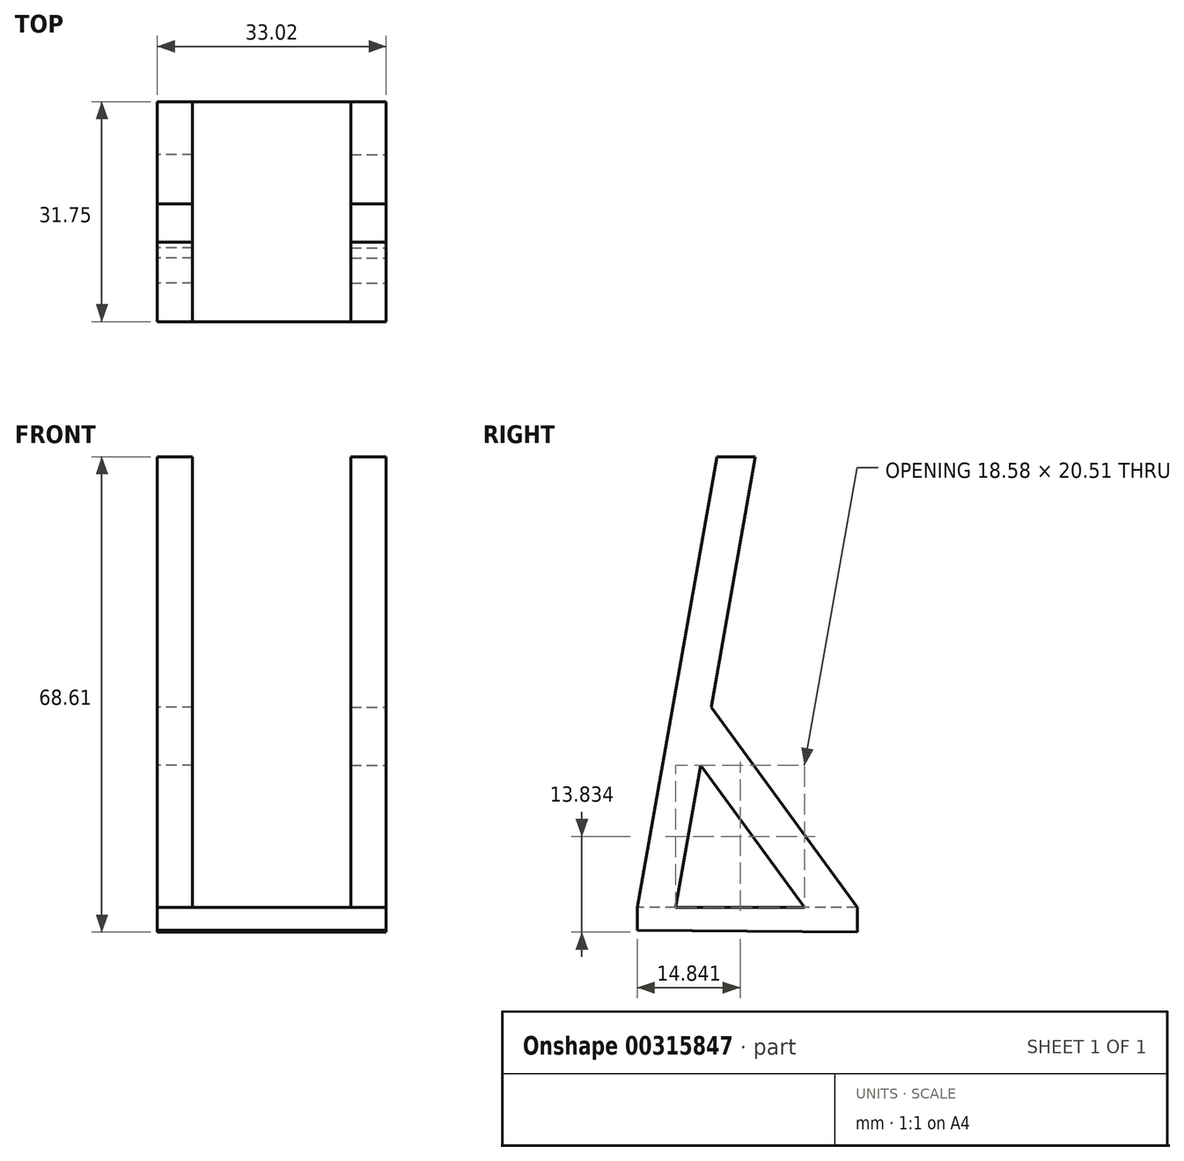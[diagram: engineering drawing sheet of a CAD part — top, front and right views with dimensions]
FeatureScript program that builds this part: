
annotation { "Feature Type Name" : "Feature", "Feature Type Description" : "" }
export const myFeature = defineFeature(function(context is Context, id is Id, definition is map)
    precondition{}
    {
        {
            var Q0;
            Q0=qCreatedBy(makeId("Right.planeOp"),FACE);
            var sketch = newSketch(context, id + "F0", { "sketchPlane" : qUnion([Q0])});
            skLineSegment(sketch, "E0", {"start": v(-16.52, -8.83) * mm, "end": v(-5.05, 56.2) * mm});
            skLineSegment(sketch, "E1", {"start": v(-10.97, -8.83) * mm, "end": v(-16.52, -8.83) * mm});
            skLineSegment(sketch, "E2", {"start": v(-10.97, -8.83) * mm, "end": v(0.5, 56.2) * mm});
            skLineSegment(sketch, "E3", {"start": v(0.5, 56.2) * mm, "end": v(-5.05, 56.2) * mm});
            skLineSegment(sketch, "E4", {"start": v(-7.35, 11.68) * mm, "end": v(7.61, -8.83) * mm});
            skLineSegment(sketch, "E5", {"start": v(15.23, -8.83) * mm, "end": v(7.61, -8.83) * mm});
            skLineSegment(sketch, "E6", {"start": v(15.23, -8.83) * mm, "end": v(-5.87, 20.1) * mm});
            skLineSegment(sketch, "E7", {"start": v(-16.52, -8.83) * mm, "end": v(-16.52, -12.16) * mm});
            skLineSegment(sketch, "E8", {"start": v(15.23, -8.83) * mm, "end": v(15.23, -12.41) * mm});
            skLineSegment(sketch, "E9", {"start": v(15.23, -12.41) * mm, "end": v(-16.52, -12.16) * mm});
            skLineSegment(sketch, "E10", {"start": v(7.61, -8.83) * mm, "end": v(-10.97, -8.83) * mm});
            skSolve(sketch);
        }
        {
            var Q0;
            Q0=makeQuery(id+"F0.imprint","IMPRINT",FACE,{"disambiguationData":[TD([[makeQuery(id+"F0.imprint","IMPRINT",EDGE,{"derivedFrom":sQuery(id+"F0.wireOp",EDGE,"E1")}),1.0]])]});
            extrude(context, id + "F1", {"entities" : qUnion([Q0]), "depth" : 16.5 * mm});
        }
        {
            var Q0;
            {var subQ0=sQuery(id+"F0.wireOp",EDGE,"E4");Q0=makeQuery(id+"F0.imprint","IMPRINT",FACE,{"disambiguationData":[TD([[makeQuery(id+"F0.imprint","IMPRINT",EDGE,{"derivedFrom":subQ0}),1.0]])]});}
            var Q1;
            Q1=makeQuery(id+"F0.imprint","IMPRINT",FACE,{"disambiguationData":[TD([[makeQuery(id+"F0.imprint","IMPRINT",EDGE,{"derivedFrom":sQuery(id+"F0.wireOp",EDGE,"E0")}),-1.0]])]});
            extrude(context, id + "F2", {"entities" : qUnion([Q0, Q1]), "operationType" : NewBodyOperationType.ADD, "depth" : 5.08 * mm});
        }
        {
            var Q0;
            Q0=makeQuery(id+"F1.opExtrude","SWEPT_BODY",BODY,{"disambiguationData":[OSD([sQuery(id+"F0.wireOp",EDGE,"E1"),sQuery(id+"F0.wireOp",EDGE,"E5"),sQuery(id+"F0.wireOp",EDGE,"E7"),sQuery(id+"F0.wireOp",EDGE,"E8"),sQuery(id+"F0.wireOp",EDGE,"E9"),sQuery(id+"F0.wireOp",EDGE,"E10")])]});
            var Q1;
            Q1=makeQuery(id+"F1.opExtrude","CAP_FACE",FACE,{"disambiguationData":[OSD([sQuery(id+"F0.wireOp",EDGE,"E1"),sQuery(id+"F0.wireOp",EDGE,"E5"),sQuery(id+"F0.wireOp",EDGE,"E7"),sQuery(id+"F0.wireOp",EDGE,"E8"),sQuery(id+"F0.wireOp",EDGE,"E9"),sQuery(id+"F0.wireOp",EDGE,"E10")])],"isStart":false});
            mirror(context, id + "F3", {"operationType" : NewBodyOperationType.ADD, "entities" : qUnion([Q0]), "mirrorPlane" : qUnion([Q1])});
        }
    });
